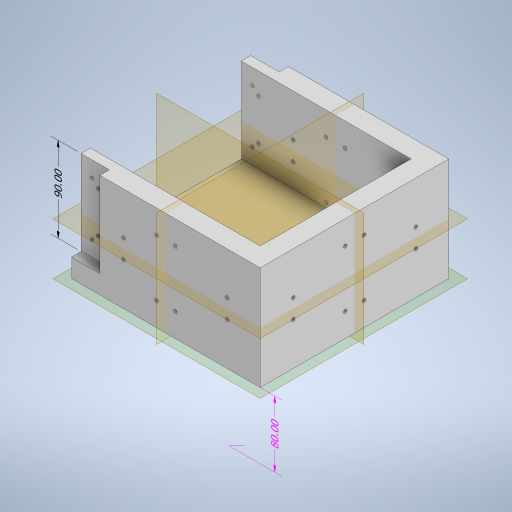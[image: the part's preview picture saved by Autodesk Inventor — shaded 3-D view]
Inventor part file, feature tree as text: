
AUTODESK INVENTOR PART (.ipt)
format: ipt  version: 2023 (Build 270158000, 158)  size: 427,520 bytes
history: native  units: mm
features: sketch x9, extrude x5, other x4, hole x4, plane x4, split x1
ambient origin geometry x8: Origin, YZ Plane, XZ Plane, XY Plane, X Axis, Y Axis, Z Axis, Center Point
bodies: Body1 (feature_tree)
feature tree (27):
  other  "Sólido1"
  other  "Anotaciones"
  extrude  "Extrusión1"  Depth=200.0mm
  hole  "Agujero1"  [1 undecoded]
  extrude  "Extrusión2"  Depth=15.0mm
  extrude  "Extrusión3"  Depth=20.0mm TaperAngle=0.0deg
  extrude  "Extrusión4"  Depth=200.0mm
  extrude  "Extrusión5"  Depth=20.0mm
  hole  "Agujero2"  [1 undecoded]
  plane  "Plano de trabajo1"
  split  "Dividir1"
  plane  "Plano de trabajo2"
  plane  "Plano de trabajo3"
  sketch  "Boceto9"  dims[d37=20.0mm d38=20.0mm]
  plane  "Plano de trabajo4"
  hole  "Agujero3"  [1 undecoded]
  hole  "Agujero4"  [1 undecoded]
  sketch  "Boceto2"  dims[d7=15.0mm d8=200.0mm]
  sketch  "Boceto3"  dims[d9=10.0mm d10=0.0mm]
  sketch  "Boceto4"  dims[d12=1.75mm d13=1.75mm d14=1.75mm d15=1.75mm d16=10.0mm d17=10.0mm d19=30.0mm]
  sketch  "Boceto5"  dims[d20=3.5mm d21=6.0mm d22=4.0mm d23=2.0mm d24=90.0deg d25=8.0mm d26=20.594885mm d27=15.0mm]
  sketch  "Boceto6"  dims[d28=20.0mm d29=80.0mm d30=0.0mm]
  sketch  "Boceto7"  dims[d31=48.0mm d32=200.0mm]
  sketch  "Boceto8"  dims[d33=110.0mm d34=0.0mm d36=20.0mm]
  sketch  "Boceto10"  dims[d39=90.0mm d40=0.0mm d42=10.0mm d43=30.0mm d44=0.0mm d46=1.75mm d47=1.75mm d48=1.75mm d49=1.75mm d50=10.0mm d51=10.0mm d52=15.0mm d56=3.5mm d57=6.0mm d58=4.0mm d59=2.0mm d60=90.0deg d61=8.0mm d62=20.594885mm d63=10.0mm d65=10.0mm d66=10.0mm d67=31.75mm d70=15.0mm d74=200.0mm d78=20.0mm d82=90.0deg d83=10.0mm d84=30.0mm d85=5.0mm d86=5.0mm d87=5.0mm d88=5.0mm d89=20.0mm d91=30.0mm d92=5.0mm d93=5.0mm d94=3.5mm d95=5.0mm d96=5.0mm d97=5.0mm d98=5.0mm d99=5.0mm d100=20.0mm d101=3.5mm d102=6.0mm d103=4.0mm d104=2.0mm d105=90.0deg d106=8.0mm d107=20.594885mm d108=10.0mm d109=30.0mm d110=5.0mm d111=5.0mm d112=5.0mm d113=5.0mm d114=5.0mm d115=5.0mm d116=3.5mm d117=5.0mm d118=5.0mm d119=5.0mm d120=5.0mm d121=5.0mm d122=30.0mm d123=30.0mm d124=3.5mm d125=6.0mm d126=4.0mm d127=2.0mm d128=90.0deg d129=8.0mm d130=20.594885mm d75=1.454734mm d76=6.982969mm d77=80.0mm d79=4.097996mm d80=1.406125mm d81=90.0mm]
  other  "Cota lineal 2"
  other  "Cota lineal 3"
note: 4 required parameter values undecoded (feature->parameter linkage not recoverable at this tier; creation-order binding heuristic only, values carry confidence <= 0.55)
